# Revit family: DV51CH BIM File
name_source: partatom
category: Mechanical Equipment
units: mm (PartAtom-declared; Revit-internal decimal feet)

## family parameters
Always vertical = Yes
Classification = None
Cut with Voids When Loaded = No
Maintain Annotation Orientation = No
Part Type = Normal
Room Calculation Point = No
Round Connector Dimension = Use Diameter
Shared = No
Work Plane-Based = No

## types (2) — shared parameters
BBVIS = No
BH = 819 mm  [stored 2.68701 ft]
CAT = No
CPH = 20 mm  [stored 0.0656168 ft]
CPL = 215 mm  [stored 0.705381 ft]
CenSd_EPR_6 = 26 mm  [stored 0.0853018 ft]
D = 125 mm
DEC = 81 mm  [stored 0.265748 ft]
DEX = 377 mm  [stored 1.23688 ft]
DEXY = 145 mm  [stored 0.475722 ft]
DOC = 518 mm  [stored 1.69948 ft]
DR = 6 mm  [stored 0.019685 ft]
DR1 = 12 mm
DSC = 222 mm
DSCY = 105 mm  [stored 0.344488 ft]
D_2 = 63 mm
Description = Ventilation unit
E = 110 mm
ENBL350 = No
EPR = 30 mm  [stored 0.0984252 ft]
ER = 26 mm  [stored 0.0853018 ft]
ER1 = 20 mm  [stored 0.0656168 ft]
H1 = 668 mm  [stored 2.1916 ft]
HB = 648 mm  [stored 2.12598 ft]
HP = 658 mm  [stored 2.15879 ft]
HP1 = 339 mm  [stored 1.1122 ft]
HP2 = 788 mm
HP3 = 425 mm  [stored 1.39436 ft]
L = 598 mm  [stored 1.96194 ft]
L1 = 597 mm  [stored 1.95866 ft]
L2 = 595 mm  [stored 1.9521 ft]
LD = 90 mm
LLDAndHLD = Yes
LLDONLY = Yes
L_2 = 299 mm  [stored 0.980971 ft]
MC Enable LOD 200 = No
MC Enable LOD 350 = No
MC Material1 MAIN_MODEL = MC_255_255_255_0_50
MC Material12 MAIN_MODEL = MC_128_128_128_0_50
MC Material13 MAIN_MODEL = MC_255_255_255_60_50
MC Material2 MAIN_MODEL = MC_191_191_191_0_50
MC Material4 MAIN_MODEL = MC_0_0_0_0_50
MC Product Code = DV51CH Adroit with cooker hood
Manufacturer = Airflow
QmdConnectorList = 221;D;231;D;241;D;251;D
RS = 63 mm
URL = https://www.airflow.com
VIS0 = No
W = 339 mm  [stored 1.1122 ft]
W1 = 368 mm  [stored 1.20735 ft]
W2 = 325 mm  [stored 1.06627 ft]
W2_2 = 163 mm
W_2 = 170 mm
zero-valued in all types: Default Elevation

## per-type parameters (varying)
| type | Airflow part no |
| DV51CH (R) | 90001174, 90001172 |
| DV51CH (L) | 90001175, 90001173 |

note: [stored X ft] marks values corroborated as IEEE doubles in the binary element streams (Revit-internal decimal feet)

## geometry (parser evidence)
native form markers: Sweep x3
no freeform markers — native parametric forms only
